# Revit family: Садовая розетка
name_source: partatom
category: Осветительные приборы
units: mm (PartAtom-declared; Revit-internal decimal feet)

## family parameters
Всегда вертикально = Да
Источник света = Нет
На основе рабочей плоскости = Нет
Общий = Нет
При загрузке вырезать с полостями = Нет
Размер круглого соединителя = Использовать диаметр
Тип детали = Нормальный
Точка расчета площади = Нет

## types (4) — shared parameters
ADSK_URL страницы изделия = https://www.allfresco.ru
ADSK_Единица измерения = шт.
ADSK_Завод-изготовитель = ALFRESCO
ADSK_Количество фаз = 2
ADSK_Модель = Садовая розетка СР
ADSK_Напряжение = 220 В
ADSK_Номинальная мощность = 0 Вт
ADSK_Полная мощность = 0 В·А
ADSK_Ток = 0 А
ADSK_Фактическая мощность = 0 Вт
ADSK_Энергоэффективность = 0 лм/Вт
D_фланец отверстия = 14 мм
D_шапка конус верх = 1 мм
H_дверка = 200 мм
H_конечной точки = 1500 мм
H_табличка = 104 мм
H_фланец = 4 мм
IP Class = IP 67
L_отступ до конечной точки = 1500 мм
L_отступ до центра = 1000 мм
L_табличка = 57 мм
R_фланец скругление = 10 мм
S1_фланец = 190 мм
S2_фланец = 150 мм
S_полстолба = 50 мм
S_табличка = 52 мм
S_шапка = 120 мм
S_шапка конус низ = 101 мм
h_табличка = 38 мм
h_шапка = 49 мм
Блок аварийного питания = Нет
Класс защиты = 1
Класс пожароопасности = F (устройства предназначены для установки непосредственно на поверхность из нормально воспламеняемых материалов)
Климатическая зона = УХЛ1
Короб_Диаметр = 20 мм
Корпус светильника = Сталь, окрашенная, темно-серая
Материал рассеивателя = -
Область использования = Парки, скверы, общественные пространства, городская инфраструктура
Полная установленная мощность = 0 В·А
Рассеиватель = Материал рассеивателя
Таблица выбора = Таблица параметров светильников_par3_v1
Температура эксплуатации = -40 +50
Тип ИС = _
Тип КСС = _
Тип ПРА = -
Тип продукции = Садовая розетка
Цветоывая температура = -
zero-valued in all types: ADSK_Количество фаз числовое, ADSK_Коэффициент мощности

## per-type parameters (varying)
| type | ADSK_Артикул | ADSK_Масса | ADSK_Масса_Текст | ADSK_Наименование | ADSK_Размер_Высота | H_полное | h_дверка | без автомата | с автоматом |
| СР1 Садовая розетка СР 0,55(К150-4М12+100х100) под 1 розетку | СР1 | 7 | 7 | СР1 Садовая розетка СР 0.55(К150-4М12+100х100) под 1 розетку | 550 мм | 549 мм | 250 мм | Да | Нет |
| СР2 Садовая розетка СР 0,55(К150-4М12+100х100) под 2 розетки | СР2 | 7 | 7 | СР2 Садовая розетка СР 0.55(К150-4М12+100х100) под 2 розетки | 550 мм | 549 мм | 250 мм | Да | Нет |
| СР3 Садовая розетка СР 0,7(К150-4М12+100х100) с автоматом под 1 розетку | СР3 | 9 | 9 | СР3 Садовая розетка СР 0.7(К150-4М12+100х100) с автоматом под 1 розетку | 700 мм | 699 мм | 400 мм | Нет | Да |
| СР4 Садовая розетка СР 0,7(К150-4М12+100х100) с автоматом под 2 розетки | СР4 | 9 | 9 | СР4 Садовая розетка СР 0.7(К150-4М12+100х100) с автоматом под 2 розетки | 700 мм | 699 мм | 400 мм | Нет | Да |

## geometry (parser evidence)
native form markers: Blend x4
no freeform markers — native parametric forms only
